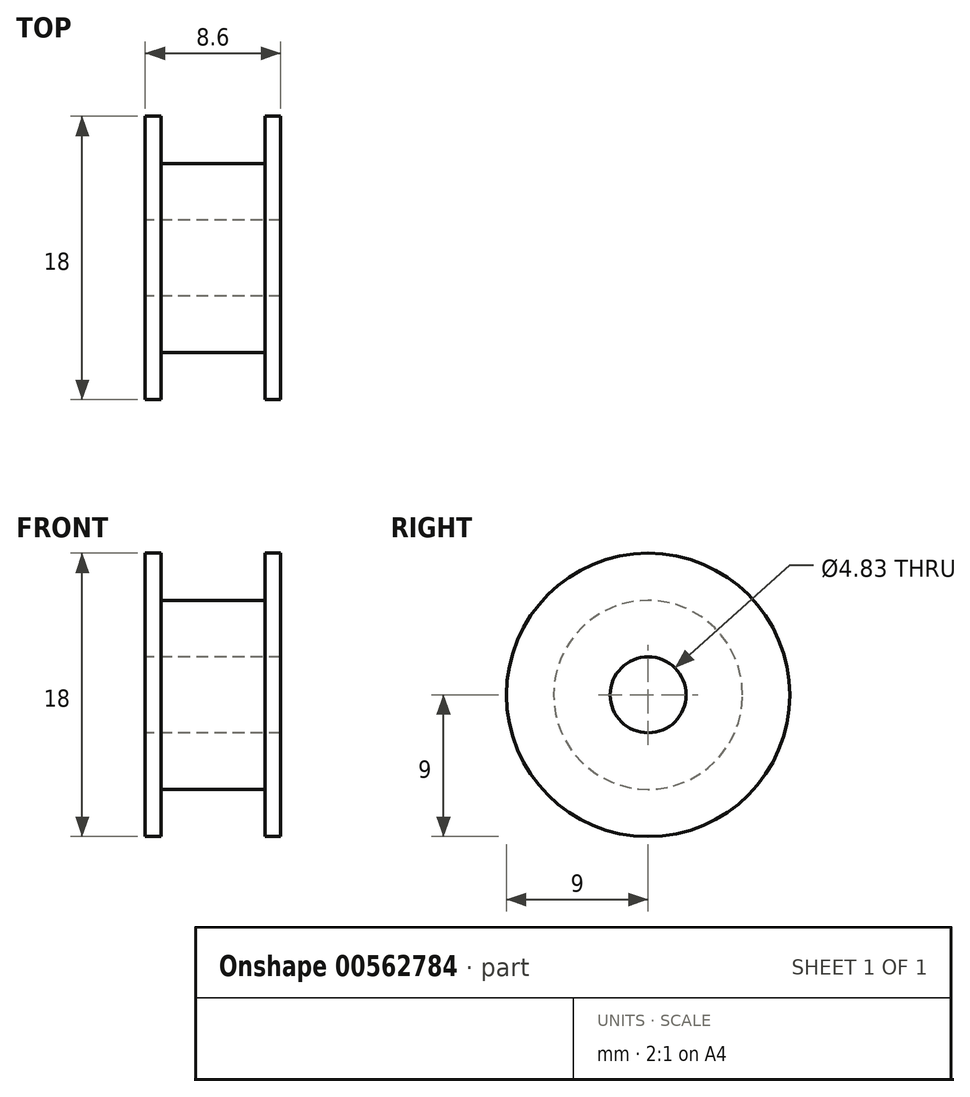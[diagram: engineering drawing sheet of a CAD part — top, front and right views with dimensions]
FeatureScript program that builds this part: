
annotation { "Feature Type Name" : "Feature", "Feature Type Description" : "" }
export const myFeature = defineFeature(function(context is Context, id is Id, definition is map)
    precondition{}
    {
        {
            var Q0;
            Q0=qCreatedBy(makeId("Front.planeOp"),FACE);
            var sketch = newSketch(context, id + "F0", { "sketchPlane" : qUnion([Q0])});
            skLineSegment(sketch, "E0", {"start": v(0, 0) * mm, "end": v(6.6, 0) * mm, "construction": true});
            skLineSegment(sketch, "E1.top", {"start": v(6.6, 6) * mm, "end": v(0, 6) * mm});
            skLineSegment(sketch, "E2.bottom", {"start": v(6.6, 0) * mm, "end": v(7.6, 0) * mm});
            skLineSegment(sketch, "E2.top", {"start": v(6.6, 9) * mm, "end": v(7.6, 9) * mm});
            skLineSegment(sketch, "E2.left", {"start": v(6.6, 6) * mm, "end": v(6.6, 9) * mm});
            skLineSegment(sketch, "E2.right", {"start": v(7.6, 0) * mm, "end": v(7.6, 9) * mm});
            skLineSegment(sketch, "E3", {"start": v(3.3, 6) * mm, "end": v(3.3, 0) * mm, "construction": true});
            skLineSegment(sketch, "E4.MirrorCS", {"start": v(0, 0) * mm, "end": v(-1, 0) * mm});
            skLineSegment(sketch, "E5.MirrorCS", {"start": v(0, 9) * mm, "end": v(-1, 9) * mm});
            skLineSegment(sketch, "E6.MirrorCS", {"start": v(0, 6) * mm, "end": v(0, 9) * mm});
            skLineSegment(sketch, "E7.MirrorCS", {"start": v(6.6, 0) * mm, "end": v(0, 0) * mm});
            skLineSegment(sketch, "E8.MirrorCS", {"start": v(-1, 0) * mm, "end": v(-1, 9) * mm});
            skLineSegment(sketch, "E9.MirrorCS", {"start": v(0, 6) * mm, "end": v(6.6, 6) * mm});
            skSolve(sketch);
        }
        {
            var Q0;
            Q0 = qSketchRegion(id + "F0", true);
            var Q1;
            Q1=sQuery(id+"F0.wireOp",EDGE,"E7.MirrorCS");
            revolve(context, id + "F1", {"entities" : qUnion([Q0]), "axis" : qUnion([Q1]), "revolveType" : RevolveType.FULL});
        }
        {
            var Q0;
            Q0=makeQuery(id+"F1.opRevolve","SWEPT_FACE",FACE,{"disambiguationData":[OSD([sQuery(id+"F0.wireOp",EDGE,"E8.MirrorCS")])]});
            var sketch = newSketch(context, id + "F2", { "sketchPlane" : qUnion([Q0])});
            skCircle(sketch, "E10", {"center": v(0, 0) * mm, "radius": 2.41 * mm});
            skSolve(sketch);
        }
        {
            var Q0;
            Q0 = qSketchRegion(id + "F2", true);
            extrude(context, id + "F3", {"entities" : qUnion([Q0]), "operationType" : NewBodyOperationType.REMOVE, "oppositeDirection" : true, "depth" : 25.4 * mm, "offsetDistance" : 25.4 * mm});
        }
    });
